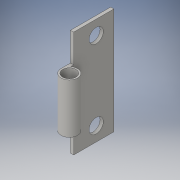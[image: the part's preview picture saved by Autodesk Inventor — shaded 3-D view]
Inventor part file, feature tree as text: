
AUTODESK INVENTOR PART (.ipt)
format: ipt  version: 2016 (Build 200138000, 138)  size: 134,144 bytes
history: native  units: in
note: dims shown in document units (in); Inventor stores cm internally (conversion verified against a paired STEP export)
features: extrude x4, sketch x4
ambient origin geometry x8: Origin, YZ Plane, XZ Plane, XY Plane, X Axis, Y Axis, Z Axis, Center Point
bodies: Solid1 (feature_tree)
feature tree (8):
  extrude  "Extrusion1"  Depth=0.233in
  sketch  "Sketch2"  dims[d2=0.7in d3=0.045in]
  extrude  "Extrusion2"  Depth=0.045in
  extrude  "Extrusion3"  Depth=1.5in
  sketch  "Sketch1"  dims[d0=0.188in d1=0.233in]
  sketch  "Sketch3"  dims[d4=1.5in d5=0.0in d6=0.3436in]
  extrude  "Extrusion4"  Depth=1.5in
  sketch  "Sketch4"  dims[d7=0.2696in d8=0.1805in d9=0.1337in d10=0.4in d11=0.0in d12=0.4in d13=0.0in d14=0.2in d15=0.2in d16=0.2in d17=0.25in d19=0.0in d20=0.7in d21=0.5513in d22=0.5513in d23=0.6432in d24=1.5in]
